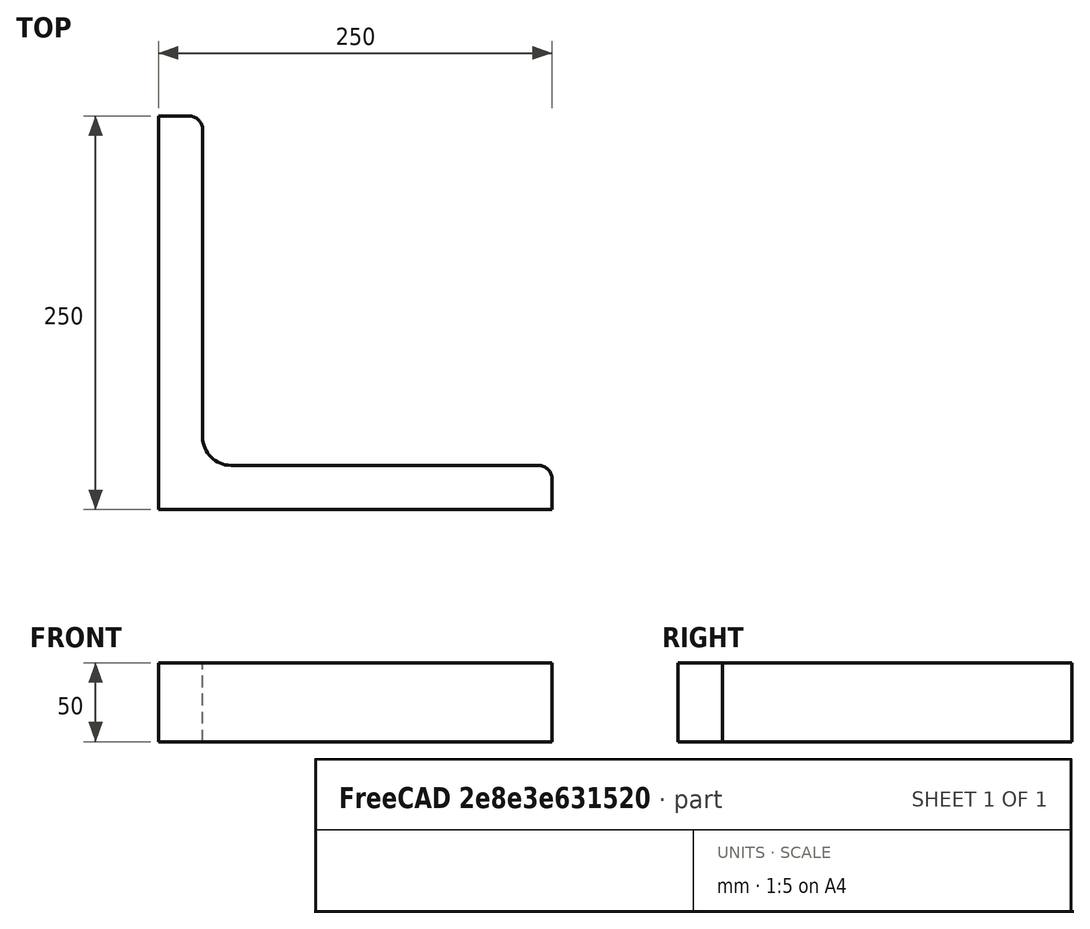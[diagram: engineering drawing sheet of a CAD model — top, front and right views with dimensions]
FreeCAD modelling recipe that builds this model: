
FCSTD DOCUMENT  (FreeCAD 0.15R4671 (Git))
Label: Angle Bar L250x250x28 EN10056 S235JR
License: All rights reserved
LicenseURL: http://en.wikipedia.org/wiki/All_rights_reserved
objects: Sketcher::SketchObject×1, Part::Extrusion×1
note: 2 computed .brp shape members not serialized (recipe doc carries the construction recipe); baked Part::Feature solids carry a one-line shape summary decoded from their .brp

FEATURE [Sketcher::SketchObject] Sketch
  sketch-geometry (9):
    g0: LineSegment StartX=0 StartY=0 StartZ=0 EndX=250 EndY=0 EndZ=0
    g1: LineSegment StartX=250 StartY=0 StartZ=0 EndX=250 EndY=19 EndZ=0
    g2: LineSegment StartX=241 StartY=28 StartZ=0 EndX=46 EndY=28 EndZ=0
    g3: LineSegment StartX=0 StartY=0 StartZ=0 EndX=0 EndY=250 EndZ=0
    g4: LineSegment StartX=0 StartY=250 StartZ=0 EndX=19 EndY=250 EndZ=0
    g5: LineSegment StartX=28 StartY=241 StartZ=0 EndX=28 EndY=46 EndZ=0
    g6: ArcOfCircle CenterX=46 CenterY=46 CenterZ=0 NormalX=0 NormalY=0 NormalZ=1 Radius=18 StartAngle=3.14159 EndAngle=4.71239
    g7: ArcOfCircle CenterX=19 CenterY=241 CenterZ=0 NormalX=0 NormalY=0 NormalZ=1 Radius=9 StartAngle=0 EndAngle=1.5708
    g8: ArcOfCircle CenterX=241 CenterY=19 CenterZ=0 NormalX=0 NormalY=0 NormalZ=1 Radius=9 StartAngle=0 EndAngle=1.5708
  constraints (23):
    c: Coincident(g0,g-1)
    c: Horizontal(g0)
    c: Coincident(g1,g0)
    c: Vertical(g1)
    c: Horizontal(g2)
    c: Coincident(g3,g-1)
    c: Vertical(g3)
    c: Coincident(g4,g3)
    c: Horizontal(g4)
    c: Vertical(g5)
    c: Tangent(g5,g6) = -1.5708
    c: Tangent(g2,g6) = 1.5708
    c: Tangent(g4,g7) = 1.5708
    c: Tangent(g5,g7) = 1.5708
    c: Tangent(g2,g8) = -1.5708
    c: Tangent(g1,g8) = -1.5708
    c: DistanceX(g0) = 250
    c: DistanceY(g3) = 250
    c: DistanceY(g0,g2) = 28
    c: DistanceX(g3,g5) = 28
    c: Radius(g6) = 18
    c: Radius(g8) = 9
    c: Radius(g7) = 9
FEATURE [Part::Extrusion] Extrude  label="Angle Bar L250x250x28 EN10056 S235JR"
  Base = -> Sketch
  Dir = (0,0,50)
  Solid = true
